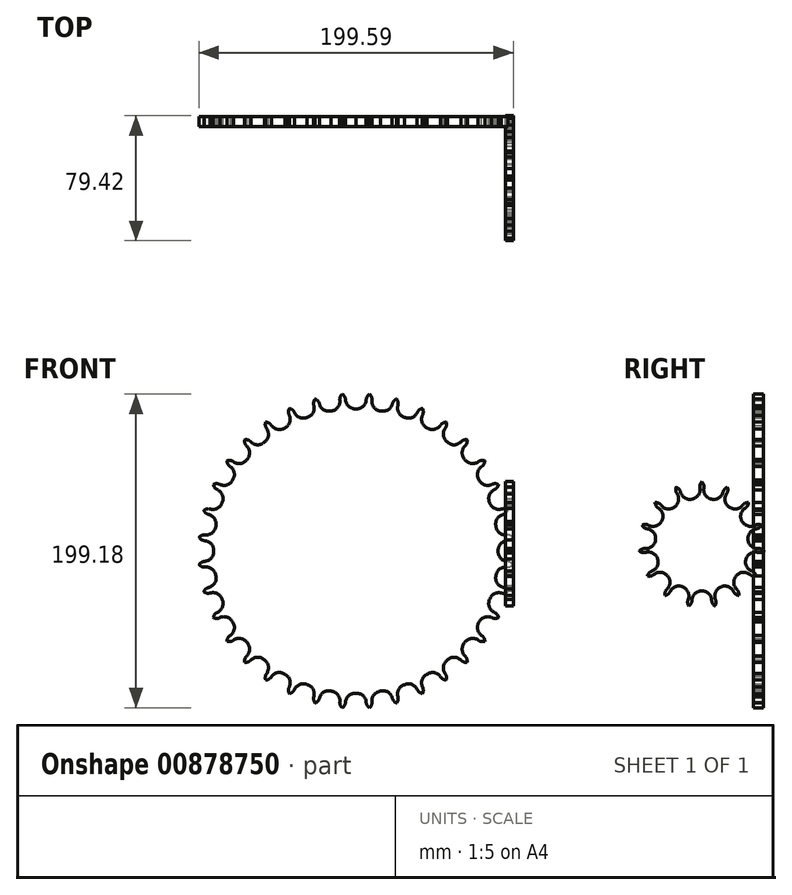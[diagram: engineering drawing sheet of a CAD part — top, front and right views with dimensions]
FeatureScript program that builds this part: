
annotation { "Feature Type Name" : "Feature", "Feature Type Description" : "" }
export const myFeature = defineFeature(function(context is Context, id is Id, definition is map)
    precondition{}
    {
        {
            var Q0;
            Q0=qCreatedBy(makeId("Right.planeOp"),FACE);
            cPlane(context, id + "F0", {"entities" : qUnion([Q0]), "cplaneType" : CPlaneType.OFFSET, "offset" : 95 * mm, "width" : 150 * mm, "height" : 150 * mm});
        }
        {
            var Q0;
            Q0=qCreatedBy(makeId("Front.planeOp"),FACE);
            var sketch = newSketch(context, id + "F1", { "sketchPlane" : qUnion([Q0])});
            skArc(sketch, "E0", {"start": v(-5.07, 74.25) * mm, "mid": v(-3.4, 71.1) * mm, "end": v(0, 70) * mm});
            skArc(sketch, "E1", {"start": v(-5.07, 74.25) * mm, "mid": v(-5.54, 75.94) * mm, "end": v(-6.79, 77.2) * mm});
            skSolve(sketch);
        }
        {
            var Q0;
            Q0=qCreatedBy(makeId("Front.planeOp"),FACE);
            var sketch = newSketch(context, id + "F2", { "sketchPlane" : qUnion([Q0])});
            skArc(sketch, "E2.0", {"start": v(20.63, -71.5) * mm, "mid": v(21.13, -67.97) * mm, "end": v(23.94, -65.78) * mm});
            skArc(sketch, "E2.1", {"start": v(7.9, -74) * mm, "mid": v(9, -70.6) * mm, "end": v(12.16, -68.94) * mm});
            skArc(sketch, "E2.2", {"start": v(51.6, -53.62) * mm, "mid": v(48.3, -52.28) * mm, "end": v(45, -53.62) * mm});
            skArc(sketch, "E2.3", {"start": v(68.04, 30.15) * mm, "mid": v(65.65, 27.5) * mm, "end": v(65.78, 23.94) * mm});
            skArc(sketch, "E2.4", {"start": v(-41.5, -61.77) * mm, "mid": v(-38.49, -59.87) * mm, "end": v(-35, -60.62) * mm});
            skArc(sketch, "E2.5", {"start": v(-17.88, -72.24) * mm, "mid": v(-15.69, -69.43) * mm, "end": v(-12.16, -68.94) * mm});
            skArc(sketch, "E2.6", {"start": v(-72.24, -17.88) * mm, "mid": v(-69.43, -15.69) * mm, "end": v(-68.94, -12.16) * mm});
            skArc(sketch, "E2.7", {"start": v(30.15, 68.04) * mm, "mid": v(27.5, 65.65) * mm, "end": v(23.94, 65.78) * mm});
            skArc(sketch, "E2.8", {"start": v(51.6, 53.62) * mm, "mid": v(48.3, 52.28) * mm, "end": v(45, 53.62) * mm});
            skArc(sketch, "E2.9", {"start": v(-74, 7.9) * mm, "mid": v(-70.6, 9) * mm, "end": v(-68.94, 12.16) * mm});
            skArc(sketch, "E2.10", {"start": v(43.84, -60.13) * mm, "mid": v(43.1, -56.64) * mm, "end": v(45, -53.62) * mm});
            skArc(sketch, "E2.11", {"start": v(32.74, 66.83) * mm, "mid": v(32.6, 63.27) * mm, "end": v(35, 60.62) * mm});
            skArc(sketch, "E2.12", {"start": v(-41.5, 61.77) * mm, "mid": v(-38.49, 59.87) * mm, "end": v(-35, 60.62) * mm});
            skArc(sketch, "E2.13", {"start": v(68.04, -30.15) * mm, "mid": v(65.65, -27.5) * mm, "end": v(65.78, -23.94) * mm});
            skArc(sketch, "E2.14", {"start": v(-61.77, -41.5) * mm, "mid": v(-59.87, -38.49) * mm, "end": v(-60.62, -35) * mm});
            skArc(sketch, "E2.15", {"start": v(-53.62, -51.6) * mm, "mid": v(-52.28, -48.3) * mm, "end": v(-53.62, -45) * mm});
            skArc(sketch, "E2.16", {"start": v(61.77, -41.5) * mm, "mid": v(59.87, -38.49) * mm, "end": v(60.62, -35) * mm});
            skArc(sketch, "E2.17", {"start": v(-43.84, -60.13) * mm, "mid": v(-43.1, -56.64) * mm, "end": v(-45, -53.62) * mm});
            skArc(sketch, "E2.18", {"start": v(-5.07, -74.25) * mm, "mid": v(-3.4, -71.1) * mm, "end": v(0, -70) * mm});
            skArc(sketch, "E2.19", {"start": v(53.62, -51.6) * mm, "mid": v(52.28, -48.3) * mm, "end": v(53.62, -45) * mm});
            skArc(sketch, "E2.20", {"start": v(41.5, 61.77) * mm, "mid": v(38.49, 59.87) * mm, "end": v(35, 60.62) * mm});
            skArc(sketch, "E2.21", {"start": v(53.62, 51.6) * mm, "mid": v(52.28, 48.3) * mm, "end": v(53.62, 45) * mm});
            skArc(sketch, "E2.22", {"start": v(-32.74, 66.83) * mm, "mid": v(-32.6, 63.27) * mm, "end": v(-35, 60.62) * mm});
            skArc(sketch, "E2.23", {"start": v(-60.13, 43.84) * mm, "mid": v(-56.64, 43.1) * mm, "end": v(-53.62, 45) * mm});
            skArc(sketch, "E2.24", {"start": v(17.88, -72.24) * mm, "mid": v(15.69, -69.43) * mm, "end": v(12.16, -68.94) * mm});
            skArc(sketch, "E2.25", {"start": v(60.13, 43.84) * mm, "mid": v(56.64, 43.1) * mm, "end": v(53.62, 45) * mm});
            skArc(sketch, "E2.26", {"start": v(72.24, -17.88) * mm, "mid": v(69.43, -15.69) * mm, "end": v(68.94, -12.16) * mm});
            skArc(sketch, "E2.27", {"start": v(-7.9, -74) * mm, "mid": v(-9, -70.6) * mm, "end": v(-12.16, -68.94) * mm});
            skArc(sketch, "E2.28", {"start": v(-66.83, 32.74) * mm, "mid": v(-63.27, 32.6) * mm, "end": v(-60.62, 35) * mm});
            skArc(sketch, "E2.29", {"start": v(-20.63, -71.5) * mm, "mid": v(-21.13, -67.97) * mm, "end": v(-23.94, -65.78) * mm});
            skArc(sketch, "E2.30", {"start": v(61.77, 41.5) * mm, "mid": v(59.87, 38.49) * mm, "end": v(60.62, 35) * mm});
            skArc(sketch, "E2.31", {"start": v(74.25, -5.07) * mm, "mid": v(71.1, -3.4) * mm, "end": v(70, 0) * mm});
            skArc(sketch, "E2.32", {"start": v(-72.24, 17.88) * mm, "mid": v(-69.43, 15.69) * mm, "end": v(-68.94, 12.16) * mm});
            skArc(sketch, "E2.33", {"start": v(-32.74, -66.83) * mm, "mid": v(-32.6, -63.27) * mm, "end": v(-35, -60.62) * mm});
            skArc(sketch, "E2.34", {"start": v(-74, -7.9) * mm, "mid": v(-70.6, -9) * mm, "end": v(-68.94, -12.16) * mm});
            skArc(sketch, "E2.35", {"start": v(-68.04, 30.15) * mm, "mid": v(-65.65, 27.5) * mm, "end": v(-65.78, 23.94) * mm});
            skArc(sketch, "E2.36", {"start": v(71.5, 20.63) * mm, "mid": v(67.97, 21.13) * mm, "end": v(65.78, 23.94) * mm});
            skArc(sketch, "E2.37", {"start": v(-71.5, -20.63) * mm, "mid": v(-67.97, -21.13) * mm, "end": v(-65.78, -23.94) * mm});
            skArc(sketch, "E2.38", {"start": v(60.13, -43.84) * mm, "mid": v(56.64, -43.1) * mm, "end": v(53.62, -45) * mm});
            skArc(sketch, "E2.39", {"start": v(41.5, -61.77) * mm, "mid": v(38.49, -59.87) * mm, "end": v(35, -60.62) * mm});
            skArc(sketch, "E2.40", {"start": v(-61.77, 41.5) * mm, "mid": v(-59.87, 38.49) * mm, "end": v(-60.62, 35) * mm});
            skArc(sketch, "E2.41", {"start": v(43.84, 60.13) * mm, "mid": v(43.1, 56.64) * mm, "end": v(45, 53.62) * mm});
            skArc(sketch, "E2.42", {"start": v(-66.83, -32.74) * mm, "mid": v(-63.27, -32.6) * mm, "end": v(-60.62, -35) * mm});
            skArc(sketch, "E2.43", {"start": v(71.5, -20.63) * mm, "mid": v(67.97, -21.13) * mm, "end": v(65.78, -23.94) * mm});
            skArc(sketch, "E2.44", {"start": v(-51.6, 53.62) * mm, "mid": v(-48.3, 52.28) * mm, "end": v(-45, 53.62) * mm});
            skArc(sketch, "E2.45", {"start": v(-17.88, 72.24) * mm, "mid": v(-15.69, 69.43) * mm, "end": v(-12.16, 68.94) * mm});
            skArc(sketch, "E2.46", {"start": v(72.24, 17.88) * mm, "mid": v(69.43, 15.69) * mm, "end": v(68.94, 12.16) * mm});
            skArc(sketch, "E2.47", {"start": v(66.83, 32.74) * mm, "mid": v(63.27, 32.6) * mm, "end": v(60.62, 35) * mm});
            skArc(sketch, "E2.48", {"start": v(-74.25, -5.07) * mm, "mid": v(-71.1, -3.4) * mm, "end": v(-70, 0) * mm});
            skArc(sketch, "E2.49", {"start": v(5.07, -74.25) * mm, "mid": v(3.4, -71.1) * mm, "end": v(0, -70) * mm});
            skArc(sketch, "E2.50", {"start": v(-30.15, -68.04) * mm, "mid": v(-27.5, -65.65) * mm, "end": v(-23.94, -65.78) * mm});
            skArc(sketch, "E2.51", {"start": v(30.15, -68.04) * mm, "mid": v(27.5, -65.65) * mm, "end": v(23.94, -65.78) * mm});
            skArc(sketch, "E2.52", {"start": v(-20.63, 71.5) * mm, "mid": v(-21.13, 67.97) * mm, "end": v(-23.94, 65.78) * mm});
            skArc(sketch, "E2.53", {"start": v(-53.62, 51.6) * mm, "mid": v(-52.28, 48.3) * mm, "end": v(-53.62, 45) * mm});
            skArc(sketch, "E2.54", {"start": v(-51.6, -53.62) * mm, "mid": v(-48.3, -52.28) * mm, "end": v(-45, -53.62) * mm});
            skArc(sketch, "E2.55", {"start": v(-60.13, -43.84) * mm, "mid": v(-56.64, -43.1) * mm, "end": v(-53.62, -45) * mm});
            skArc(sketch, "E2.56", {"start": v(74, 7.9) * mm, "mid": v(70.6, 9) * mm, "end": v(68.94, 12.16) * mm});
            skArc(sketch, "E2.57", {"start": v(-74.25, 5.07) * mm, "mid": v(-71.1, 3.4) * mm, "end": v(-70, 0) * mm});
            skArc(sketch, "E2.58", {"start": v(74, -7.9) * mm, "mid": v(70.6, -9) * mm, "end": v(68.94, -12.16) * mm});
            skArc(sketch, "E2.59", {"start": v(-43.84, 60.13) * mm, "mid": v(-43.1, 56.64) * mm, "end": v(-45, 53.62) * mm});
            skArc(sketch, "E2.60", {"start": v(-30.15, 68.04) * mm, "mid": v(-27.5, 65.65) * mm, "end": v(-23.94, 65.78) * mm});
            skArc(sketch, "E2.61", {"start": v(-71.5, 20.63) * mm, "mid": v(-67.97, 21.13) * mm, "end": v(-65.78, 23.94) * mm});
            skArc(sketch, "E2.62", {"start": v(32.74, -66.83) * mm, "mid": v(32.6, -63.27) * mm, "end": v(35, -60.62) * mm});
            skArc(sketch, "E2.63", {"start": v(-68.04, -30.15) * mm, "mid": v(-65.65, -27.5) * mm, "end": v(-65.78, -23.94) * mm});
            skArc(sketch, "E2.64", {"start": v(74.25, 5.07) * mm, "mid": v(71.1, 3.4) * mm, "end": v(70, 0) * mm});
            skArc(sketch, "E2.65", {"start": v(66.83, -32.74) * mm, "mid": v(63.27, -32.6) * mm, "end": v(60.62, -35) * mm});
            skArc(sketch, "E3.0", {"start": v(17.88, 72.24) * mm, "mid": v(15.69, 69.43) * mm, "end": v(12.16, 68.94) * mm});
            skArc(sketch, "E3.1", {"start": v(5.07, 74.25) * mm, "mid": v(3.4, 71.1) * mm, "end": v(0, 70) * mm});
            skArc(sketch, "E3.2", {"start": v(-7.9, 74) * mm, "mid": v(-9, 70.6) * mm, "end": v(-12.16, 68.94) * mm});
            skArc(sketch, "E3.3", {"start": v(-5.07, 74.25) * mm, "mid": v(-3.4, 71.1) * mm, "end": v(0, 70) * mm});
            skArc(sketch, "E3.4", {"start": v(7.9, 74) * mm, "mid": v(9, 70.6) * mm, "end": v(12.16, 68.94) * mm});
            skArc(sketch, "E3.6", {"start": v(20.63, 71.5) * mm, "mid": v(21.13, 67.97) * mm, "end": v(23.94, 65.78) * mm});
            skArc(sketch, "E4.0", {"start": v(20.63, 71.5) * mm, "mid": v(20.76, 73.26) * mm, "end": v(20.02, 74.86) * mm});
            skArc(sketch, "E5.0", {"start": v(17.88, 72.24) * mm, "mid": v(18.65, 73.83) * mm, "end": v(20.09, 74.84) * mm});
            skArc(sketch, "E6.0", {"start": v(7.9, 74) * mm, "mid": v(7.73, 75.75) * mm, "end": v(6.72, 77.2) * mm});
            skArc(sketch, "E7.0", {"start": v(5.07, 74.25) * mm, "mid": v(5.54, 75.94) * mm, "end": v(6.79, 77.2) * mm});
            skPoint(sketch, "E8.0", {"position": v(0, 0) * mm});
            skArc(sketch, "E9.0", {"start": v(-5.07, 74.25) * mm, "mid": v(-5.54, 75.94) * mm, "end": v(-6.79, 77.2) * mm});
            skArc(sketch, "E10.0", {"start": v(-7.9, 74) * mm, "mid": v(-7.73, 75.75) * mm, "end": v(-6.72, 77.2) * mm});
            skArc(sketch, "E11.0", {"start": v(-17.88, 72.24) * mm, "mid": v(-18.65, 73.83) * mm, "end": v(-20.09, 74.84) * mm});
            skArc(sketch, "E12.0", {"start": v(-20.63, 71.5) * mm, "mid": v(-20.76, 73.26) * mm, "end": v(-20.02, 74.86) * mm});
            skPoint(sketch, "E13.0", {"position": v(-31.19, 69.46) * mm});
            skArc(sketch, "E14.0", {"start": v(-30.15, 68.04) * mm, "mid": v(-31.18, 69.47) * mm, "end": v(-32.78, 70.21) * mm});
            skArc(sketch, "E15.0", {"start": v(-32.74, 66.83) * mm, "mid": v(-33.17, 68.54) * mm, "end": v(-32.72, 70.24) * mm});
            skArc(sketch, "E16.0", {"start": v(-41.5, 61.77) * mm, "mid": v(-42.77, 63) * mm, "end": v(-44.47, 63.45) * mm});
            skArc(sketch, "E17.0", {"start": v(-43.84, 60.13) * mm, "mid": v(-44.57, 61.74) * mm, "end": v(-44.42, 63.5) * mm});
            skArc(sketch, "E18.0", {"start": v(30.15, 68.04) * mm, "mid": v(31.18, 69.47) * mm, "end": v(32.78, 70.21) * mm});
            skArc(sketch, "E19.0", {"start": v(32.74, 66.83) * mm, "mid": v(33.17, 68.54) * mm, "end": v(32.72, 70.24) * mm});
            skArc(sketch, "E20.0", {"start": v(41.5, 61.77) * mm, "mid": v(42.77, 63) * mm, "end": v(44.47, 63.45) * mm});
            skArc(sketch, "E21.0", {"start": v(43.84, 60.13) * mm, "mid": v(44.57, 61.74) * mm, "end": v(44.42, 63.5) * mm});
            skArc(sketch, "E22.2", {"start": v(-60.13, 43.84) * mm, "mid": v(-61.74, 44.57) * mm, "end": v(-63.5, 44.42) * mm});
            skArc(sketch, "E23.0", {"start": v(-53.62, 51.6) * mm, "mid": v(-54.61, 53.06) * mm, "end": v(-54.77, 54.82) * mm});
            skArc(sketch, "E24.0", {"start": v(-51.6, 53.62) * mm, "mid": v(-53.06, 54.61) * mm, "end": v(-54.82, 54.77) * mm});
            skArc(sketch, "E25.0", {"start": v(-61.77, 41.5) * mm, "mid": v(-63, 42.77) * mm, "end": v(-63.45, 44.47) * mm});
            skArc(sketch, "E25.1", {"start": v(-66.83, 32.74) * mm, "mid": v(-68.54, 33.17) * mm, "end": v(-70.24, 32.72) * mm});
            skArc(sketch, "E25.2", {"start": v(-68.04, 30.15) * mm, "mid": v(-69.47, 31.18) * mm, "end": v(-70.21, 32.78) * mm});
            skArc(sketch, "E26.0", {"start": v(-72.24, -17.88) * mm, "mid": v(-73.83, -18.65) * mm, "end": v(-74.84, -20.09) * mm});
            skArc(sketch, "E26.1", {"start": v(-68.04, -30.15) * mm, "mid": v(-69.47, -31.18) * mm, "end": v(-70.21, -32.78) * mm});
            skArc(sketch, "E26.2", {"start": v(-71.5, -20.63) * mm, "mid": v(-73.26, -20.76) * mm, "end": v(-74.86, -20.02) * mm});
            skArc(sketch, "E26.3", {"start": v(-74, -7.9) * mm, "mid": v(-75.75, -7.73) * mm, "end": v(-77.2, -6.72) * mm});
            skArc(sketch, "E26.4", {"start": v(-71.5, 20.63) * mm, "mid": v(-73.26, 20.76) * mm, "end": v(-74.86, 20.02) * mm});
            skArc(sketch, "E26.5", {"start": v(-74, 7.9) * mm, "mid": v(-75.75, 7.73) * mm, "end": v(-77.2, 6.72) * mm});
            skArc(sketch, "E26.6", {"start": v(-72.24, 17.88) * mm, "mid": v(-73.83, 18.65) * mm, "end": v(-74.84, 20.09) * mm});
            skArc(sketch, "E26.7", {"start": v(-66.83, -32.74) * mm, "mid": v(-68.54, -33.17) * mm, "end": v(-70.24, -32.72) * mm});
            skArc(sketch, "E26.8", {"start": v(-74.25, -5.07) * mm, "mid": v(-75.94, -5.54) * mm, "end": v(-77.2, -6.79) * mm});
            skArc(sketch, "E26.9", {"start": v(-74.25, 5.07) * mm, "mid": v(-75.94, 5.54) * mm, "end": v(-77.2, 6.79) * mm});
            skArc(sketch, "E27.0", {"start": v(-43.84, -60.13) * mm, "mid": v(-44.57, -61.74) * mm, "end": v(-44.42, -63.5) * mm});
            skArc(sketch, "E27.1", {"start": v(30.15, -68.04) * mm, "mid": v(31.18, -69.47) * mm, "end": v(32.78, -70.21) * mm});
            skArc(sketch, "E27.2", {"start": v(5.07, -74.25) * mm, "mid": v(5.54, -75.94) * mm, "end": v(6.79, -77.2) * mm});
            skArc(sketch, "E27.3", {"start": v(41.5, -61.77) * mm, "mid": v(42.77, -63) * mm, "end": v(44.47, -63.45) * mm});
            skArc(sketch, "E27.4", {"start": v(43.84, -60.13) * mm, "mid": v(44.57, -61.74) * mm, "end": v(44.42, -63.5) * mm});
            skArc(sketch, "E27.5", {"start": v(-30.15, -68.04) * mm, "mid": v(-31.18, -69.47) * mm, "end": v(-32.78, -70.21) * mm});
            skArc(sketch, "E27.6", {"start": v(-61.77, -41.5) * mm, "mid": v(-63, -42.77) * mm, "end": v(-63.45, -44.47) * mm});
            skArc(sketch, "E27.7", {"start": v(20.63, -71.5) * mm, "mid": v(20.76, -73.26) * mm, "end": v(20.02, -74.86) * mm});
            skArc(sketch, "E27.8", {"start": v(-51.6, -53.62) * mm, "mid": v(-53.06, -54.61) * mm, "end": v(-54.82, -54.77) * mm});
            skArc(sketch, "E27.9", {"start": v(51.6, -53.62) * mm, "mid": v(53.06, -54.61) * mm, "end": v(54.82, -54.77) * mm});
            skArc(sketch, "E27.10", {"start": v(-41.5, -61.77) * mm, "mid": v(-42.77, -63) * mm, "end": v(-44.47, -63.45) * mm});
            skArc(sketch, "E27.11", {"start": v(7.9, -74) * mm, "mid": v(7.73, -75.75) * mm, "end": v(6.72, -77.2) * mm});
            skArc(sketch, "E27.12", {"start": v(53.62, -51.6) * mm, "mid": v(54.61, -53.06) * mm, "end": v(54.77, -54.82) * mm});
            skArc(sketch, "E27.13", {"start": v(17.88, -72.24) * mm, "mid": v(18.65, -73.83) * mm, "end": v(20.09, -74.84) * mm});
            skArc(sketch, "E27.14", {"start": v(-17.88, -72.24) * mm, "mid": v(-18.65, -73.83) * mm, "end": v(-20.09, -74.84) * mm});
            skArc(sketch, "E27.15", {"start": v(32.74, -66.83) * mm, "mid": v(33.17, -68.54) * mm, "end": v(32.72, -70.24) * mm});
            skArc(sketch, "E27.16", {"start": v(-7.9, -74) * mm, "mid": v(-7.73, -75.75) * mm, "end": v(-6.72, -77.2) * mm});
            skArc(sketch, "E27.17", {"start": v(61.77, -41.5) * mm, "mid": v(63, -42.77) * mm, "end": v(63.45, -44.47) * mm});
            skArc(sketch, "E27.18", {"start": v(60.13, -43.84) * mm, "mid": v(61.74, -44.57) * mm, "end": v(63.5, -44.42) * mm});
            skArc(sketch, "E27.19", {"start": v(-5.07, -74.25) * mm, "mid": v(-5.54, -75.94) * mm, "end": v(-6.79, -77.2) * mm});
            skArc(sketch, "E27.20", {"start": v(-32.74, -66.83) * mm, "mid": v(-33.17, -68.54) * mm, "end": v(-32.72, -70.24) * mm});
            skArc(sketch, "E27.21", {"start": v(-53.62, -51.6) * mm, "mid": v(-54.61, -53.06) * mm, "end": v(-54.77, -54.82) * mm});
            skArc(sketch, "E27.22", {"start": v(-60.13, -43.84) * mm, "mid": v(-61.74, -44.57) * mm, "end": v(-63.5, -44.42) * mm});
            skArc(sketch, "E27.23", {"start": v(-20.63, -71.5) * mm, "mid": v(-20.76, -73.26) * mm, "end": v(-20.02, -74.86) * mm});
            skArc(sketch, "E28.0", {"start": v(74, -7.9) * mm, "mid": v(75.75, -7.73) * mm, "end": v(77.2, -6.72) * mm});
            skArc(sketch, "E28.1", {"start": v(68.04, -30.15) * mm, "mid": v(69.47, -31.18) * mm, "end": v(70.21, -32.78) * mm});
            skArc(sketch, "E28.2", {"start": v(66.83, 32.74) * mm, "mid": v(68.54, 33.17) * mm, "end": v(70.24, 32.72) * mm});
            skArc(sketch, "E28.3", {"start": v(72.24, -17.88) * mm, "mid": v(73.83, -18.65) * mm, "end": v(74.84, -20.09) * mm});
            skArc(sketch, "E28.4", {"start": v(74, 7.9) * mm, "mid": v(75.75, 7.73) * mm, "end": v(77.2, 6.72) * mm});
            skArc(sketch, "E28.5", {"start": v(71.5, 20.63) * mm, "mid": v(73.26, 20.76) * mm, "end": v(74.86, 20.02) * mm});
            skArc(sketch, "E28.6", {"start": v(71.5, -20.63) * mm, "mid": v(73.26, -20.76) * mm, "end": v(74.86, -20.02) * mm});
            skArc(sketch, "E28.7", {"start": v(74.25, -5.07) * mm, "mid": v(75.94, -5.54) * mm, "end": v(77.2, -6.79) * mm});
            skArc(sketch, "E28.8", {"start": v(66.83, -32.74) * mm, "mid": v(68.54, -33.17) * mm, "end": v(70.24, -32.72) * mm});
            skArc(sketch, "E28.9", {"start": v(74.25, 5.07) * mm, "mid": v(75.94, 5.54) * mm, "end": v(77.2, 6.79) * mm});
            skArc(sketch, "E28.10", {"start": v(68.04, 30.15) * mm, "mid": v(69.47, 31.18) * mm, "end": v(70.21, 32.78) * mm});
            skArc(sketch, "E28.11", {"start": v(72.24, 17.88) * mm, "mid": v(73.83, 18.65) * mm, "end": v(74.84, 20.09) * mm});
            skArc(sketch, "E29.0", {"start": v(51.6, 53.62) * mm, "mid": v(53.06, 54.61) * mm, "end": v(54.82, 54.77) * mm});
            skArc(sketch, "E29.1", {"start": v(53.62, 51.6) * mm, "mid": v(54.61, 53.06) * mm, "end": v(54.77, 54.82) * mm});
            skArc(sketch, "E29.2", {"start": v(78.58, 56.75) * mm, "mid": v(80.19, 57.47) * mm, "end": v(81.94, 57.32) * mm});
            skArc(sketch, "E29.3", {"start": v(61.77, 41.5) * mm, "mid": v(63, 42.77) * mm, "end": v(63.45, 44.47) * mm});
            skArc(sketch, "E29.12", {"start": v(60.13, 43.84) * mm, "mid": v(61.74, 44.57) * mm, "end": v(63.5, 44.42) * mm});
            skSolve(sketch);
        }
        {
            var Q0;
            {var subQ51=sQuery(id+"F2.wireOp",EDGE,"E2.14");Q0=makeQuery(id+"F2.imprint","IMPRINT",FACE,{"disambiguationData":[TD([[makeQuery(id+"F2.imprint","IMPRINT",EDGE,{"derivedFrom":subQ51}),-1.0]])]});}
            extrude(context, id + "F3", {"entities" : qUnion([Q0]), "depth" : 5 * mm, "offsetDistance" : 25 * mm});
        }
        {
            var Q0;
            {var subQ51=sQuery(id+"F2.wireOp",EDGE,"E2.14");Q0=makeQuery(id+"F2.imprint","IMPRINT",FACE,{"disambiguationData":[TD([[makeQuery(id+"F2.imprint","IMPRINT",EDGE,{"derivedFrom":subQ51}),-1.0]])]});}
            extrude(context, id + "F4", {"entities" : qUnion([Q0]), "operationType" : NewBodyOperationType.ADD, "depth" : 3.87 * mm, "offsetDistance" : 25 * mm});
        }
        {
            var Q0;
            Q0=makeQuery(id+"F3.opExtrude","SWEPT_BODY",BODY,{"disambiguationData":[OSD([sQuery(id+"F2.wireOp",EDGE,"E2.14"),sQuery(id+"F2.wireOp",EDGE,"E2.16"),sQuery(id+"F2.wireOp",EDGE,"E2.42"),sQuery(id+"F2.wireOp",EDGE,"E2.60"),sQuery(id+"F2.wireOp",EDGE,"E2.63"),sQuery(id+"F2.wireOp",EDGE,"E3.0"),sQuery(id+"F2.wireOp",EDGE,"E3.1"),sQuery(id+"F2.wireOp",EDGE,"E3.2"),sQuery(id+"F2.wireOp",EDGE,"E3.3"),sQuery(id+"F2.wireOp",EDGE,"E3.4"),sQuery(id+"F2.wireOp",EDGE,"E3.6"),sQuery(id+"F2.wireOp",EDGE,"E2.7"),sQuery(id+"F2.wireOp",EDGE,"E2.12"),sQuery(id+"F2.wireOp",EDGE,"E2.20"),sQuery(id+"F2.wireOp",EDGE,"E2.22"),sQuery(id+"F2.wireOp",EDGE,"E2.25"),sQuery(id+"F2.wireOp",EDGE,"E2.26"),sQuery(id+"F2.wireOp",EDGE,"E2.32"),sQuery(id+"F2.wireOp",EDGE,"E2.35"),sQuery(id+"F2.wireOp",EDGE,"E2.41"),sQuery(id+"F2.wireOp",EDGE,"E2.44"),sQuery(id+"F2.wireOp",EDGE,"E2.45"),sQuery(id+"F2.wireOp",EDGE,"E2.48"),sQuery(id+"F2.wireOp",EDGE,"E2.52"),sQuery(id+"F2.wireOp",EDGE,"E2.59"),sQuery(id+"F2.wireOp",EDGE,"E2.64"),sQuery(id+"F2.wireOp",EDGE,"E4.0"),sQuery(id+"F2.wireOp",EDGE,"E5.0"),sQuery(id+"F2.wireOp",EDGE,"E6.0"),sQuery(id+"F2.wireOp",EDGE,"E7.0"),sQuery(id+"F2.wireOp",EDGE,"E9.0"),sQuery(id+"F2.wireOp",EDGE,"E10.0"),sQuery(id+"F2.wireOp",EDGE,"E11.0"),sQuery(id+"F2.wireOp",EDGE,"E12.0"),sQuery(id+"F2.wireOp",EDGE,"E14.0"),sQuery(id+"F2.wireOp",EDGE,"E15.0"),sQuery(id+"F2.wireOp",EDGE,"E16.0"),sQuery(id+"F2.wireOp",EDGE,"E17.0"),sQuery(id+"F2.wireOp",EDGE,"E18.0"),sQuery(id+"F2.wireOp",EDGE,"E19.0"),sQuery(id+"F2.wireOp",EDGE,"E2.23"),sQuery(id+"F2.wireOp",EDGE,"E2.53"),sQuery(id+"F2.wireOp",EDGE,"E24.0"),sQuery(id+"F2.wireOp",EDGE,"E23.0"),sQuery(id+"F2.wireOp",EDGE,"E25.0"),sQuery(id+"F2.wireOp",EDGE,"E25.1"),sQuery(id+"F2.wireOp",EDGE,"E25.2"),sQuery(id+"F2.wireOp",EDGE,"E2.28"),sQuery(id+"F2.wireOp",EDGE,"E2.40"),sQuery(id+"F2.wireOp",EDGE,"E22.2"),sQuery(id+"F2.wireOp",EDGE,"E26.0"),sQuery(id+"F2.wireOp",EDGE,"E26.1"),sQuery(id+"F2.wireOp",EDGE,"E26.2"),sQuery(id+"F2.wireOp",EDGE,"E26.3"),sQuery(id+"F2.wireOp",EDGE,"E26.4"),sQuery(id+"F2.wireOp",EDGE,"E26.5"),sQuery(id+"F2.wireOp",EDGE,"E26.6"),sQuery(id+"F2.wireOp",EDGE,"E26.7"),sQuery(id+"F2.wireOp",EDGE,"E26.8"),sQuery(id+"F2.wireOp",EDGE,"E26.9"),sQuery(id+"F2.wireOp",EDGE,"E2.6"),sQuery(id+"F2.wireOp",EDGE,"E2.9"),sQuery(id+"F2.wireOp",EDGE,"E2.34"),sQuery(id+"F2.wireOp",EDGE,"E2.37"),sQuery(id+"F2.wireOp",EDGE,"E2.57"),sQuery(id+"F2.wireOp",EDGE,"E2.61"),sQuery(id+"F2.wireOp",EDGE,"E27.0"),sQuery(id+"F2.wireOp",EDGE,"E27.1"),sQuery(id+"F2.wireOp",EDGE,"E27.2"),sQuery(id+"F2.wireOp",EDGE,"E27.3"),sQuery(id+"F2.wireOp",EDGE,"E27.4"),sQuery(id+"F2.wireOp",EDGE,"E27.5"),sQuery(id+"F2.wireOp",EDGE,"E27.6"),sQuery(id+"F2.wireOp",EDGE,"E27.7"),sQuery(id+"F2.wireOp",EDGE,"E27.8"),sQuery(id+"F2.wireOp",EDGE,"E27.9"),sQuery(id+"F2.wireOp",EDGE,"E27.10"),sQuery(id+"F2.wireOp",EDGE,"E27.11"),sQuery(id+"F2.wireOp",EDGE,"E27.12"),sQuery(id+"F2.wireOp",EDGE,"E27.13"),sQuery(id+"F2.wireOp",EDGE,"E27.14"),sQuery(id+"F2.wireOp",EDGE,"E27.15"),sQuery(id+"F2.wireOp",EDGE,"E27.16"),sQuery(id+"F2.wireOp",EDGE,"E27.17"),sQuery(id+"F2.wireOp",EDGE,"E27.18"),sQuery(id+"F2.wireOp",EDGE,"E27.19"),sQuery(id+"F2.wireOp",EDGE,"E27.20"),sQuery(id+"F2.wireOp",EDGE,"E27.21"),sQuery(id+"F2.wireOp",EDGE,"E27.22"),sQuery(id+"F2.wireOp",EDGE,"E27.23"),sQuery(id+"F2.wireOp",EDGE,"E2.0"),sQuery(id+"F2.wireOp",EDGE,"E2.1"),sQuery(id+"F2.wireOp",EDGE,"E2.2"),sQuery(id+"F2.wireOp",EDGE,"E2.4"),sQuery(id+"F2.wireOp",EDGE,"E2.5"),sQuery(id+"F2.wireOp",EDGE,"E2.10"),sQuery(id+"F2.wireOp",EDGE,"E2.15"),sQuery(id+"F2.wireOp",EDGE,"E2.17"),sQuery(id+"F2.wireOp",EDGE,"E2.18"),sQuery(id+"F2.wireOp",EDGE,"E2.19"),sQuery(id+"F2.wireOp",EDGE,"E2.24"),sQuery(id+"F2.wireOp",EDGE,"E2.27"),sQuery(id+"F2.wireOp",EDGE,"E2.29"),sQuery(id+"F2.wireOp",EDGE,"E2.33"),sQuery(id+"F2.wireOp",EDGE,"E2.38"),sQuery(id+"F2.wireOp",EDGE,"E2.39"),sQuery(id+"F2.wireOp",EDGE,"E2.49"),sQuery(id+"F2.wireOp",EDGE,"E2.50"),sQuery(id+"F2.wireOp",EDGE,"E2.51"),sQuery(id+"F2.wireOp",EDGE,"E2.54"),sQuery(id+"F2.wireOp",EDGE,"E2.55"),sQuery(id+"F2.wireOp",EDGE,"E2.62"),sQuery(id+"F2.wireOp",EDGE,"E28.0"),sQuery(id+"F2.wireOp",EDGE,"E28.1"),sQuery(id+"F2.wireOp",EDGE,"E28.3"),sQuery(id+"F2.wireOp",EDGE,"E28.4"),sQuery(id+"F2.wireOp",EDGE,"E28.5"),sQuery(id+"F2.wireOp",EDGE,"E28.6"),sQuery(id+"F2.wireOp",EDGE,"E28.7"),sQuery(id+"F2.wireOp",EDGE,"E28.8"),sQuery(id+"F2.wireOp",EDGE,"E28.9"),sQuery(id+"F2.wireOp",EDGE,"E28.11"),sQuery(id+"F2.wireOp",EDGE,"E2.3"),sQuery(id+"F2.wireOp",EDGE,"E2.13"),sQuery(id+"F2.wireOp",EDGE,"E2.31"),sQuery(id+"F2.wireOp",EDGE,"E2.36"),sQuery(id+"F2.wireOp",EDGE,"E2.43"),sQuery(id+"F2.wireOp",EDGE,"E2.46"),sQuery(id+"F2.wireOp",EDGE,"E2.56"),sQuery(id+"F2.wireOp",EDGE,"E2.58"),sQuery(id+"F2.wireOp",EDGE,"E2.65"),sQuery(id+"F2.wireOp",EDGE,"E29.0"),sQuery(id+"F2.wireOp",EDGE,"E29.1"),sQuery(id+"F2.wireOp",EDGE,"E29.3"),sQuery(id+"F2.wireOp",EDGE,"E2.8"),sQuery(id+"F2.wireOp",EDGE,"E2.11"),sQuery(id+"F2.wireOp",EDGE,"E2.21"),sQuery(id+"F2.wireOp",EDGE,"E28.2"),sQuery(id+"F2.wireOp",EDGE,"E21.0"),sQuery(id+"F2.wireOp",EDGE,"E2.30"),sQuery(id+"F2.wireOp",EDGE,"E20.0"),sQuery(id+"F2.wireOp",EDGE,"E28.10"),sQuery(id+"F2.wireOp",EDGE,"E29.12"),sQuery(id+"F2.wireOp",EDGE,"E2.47")])]});
            var Q1;
            Q1=sQuery(id+"F2.wireOp",VERTEX,"E8.0");
            transform(context, id + "F5", {"entities" : qUnion([Q0]), "transformType" : TransformType.SCALE_UNIFORMLY, "scale" : 1.3, "scalePoint" : qUnion([Q1]), "makeCopy" : false});
        }
        {
            var Q0;
            Q0=qCreatedBy(makeId("Right.planeOp"),FACE);
            var sketch = newSketch(context, id + "F6", { "sketchPlane" : qUnion([Q0])});
            skArc(sketch, "E30", {"start": v(0, 36.48) * mm, "mid": v(1.7, 37.15) * mm, "end": v(2.82, 38.58) * mm});
            skArc(sketch, "E31", {"start": v(4.2, 39.72) * mm, "mid": v(3.26, 39.45) * mm, "end": v(2.82, 38.58) * mm});
            skSolve(sketch);
        }
        {
            var Q0;
            Q0=qCreatedBy(makeId("Front.planeOp"),FACE);
            var sketch = newSketch(context, id + "F7", { "sketchPlane" : qUnion([Q0])});
            skLineSegment(sketch, "E32", {"start": v(46.12, 0) * mm, "end": v(-35.6, 0) * mm});
            skSolve(sketch);
        }
        {
            var Q0;
            {var subQ0=sQuery(id+"FuSN5E2cZiAuNOm_3.wireOp",EDGE,"ce970788-27e3-47bc-be1a-0d92f62c386a.16");var subQ1=makeQuery(id+"FuSN5E2cZiAuNOm_3.imprint","INTERSECT",VERTEX,{"derivedFrom":[sQuery(id+"FuSN5E2cZiAuNOm_3.wireOp",EDGE,"57e1b842-f4a4-4b15-bf3c-e8c0f55d15c8.111"),subQ0]});Q0=makeQuery(id+"FuSN5E2cZiAuNOm_3.imprint","IMPRINT",FACE,{"disambiguationData":[TD([[makeQuery(id+"FuSN5E2cZiAuNOm_3.imprint","IMPRINT",EDGE,{"disambiguationData":[TD([[subQ1,-1.0]])],"derivedFrom":subQ0}),1.0]])]});}
            var sketch = newSketch(context, id + "F8", { "sketchPlane" : qUnion([Q0])});
            skArc(sketch, "E33.0", {"start": v(21.98, -28.21) * mm, "mid": v(20.25, -23.99) * mm, "end": v(21.93, -19.74) * mm});
            skArc(sketch, "E34.0", {"start": v(21.98, -28.21) * mm, "mid": v(23.25, -30.07) * mm, "end": v(23.47, -32.3) * mm});
            skPoint(sketch, "E35.0", {"position": v(29.43, -27) * mm});
            skPoint(sketch, "E36.0", {"position": v(29.92, -26.44) * mm});
            skLineSegment(sketch, "E37", {"start": v(29.43, -27) * mm, "end": v(29.92, -26.44) * mm});
            skLineSegment(sketch, "E38", {"start": v(29.67, -26.72) * mm, "end": v(0, 0) * mm});
            skPoint(sketch, "E39.0", {"position": v(23.77, -32.09) * mm});
            skLineSegment(sketch, "E40", {"start": v(23.17, -32.52) * mm, "end": v(23.77, -32.09) * mm});
            skLineSegment(sketch, "E41", {"start": v(23.47, -32.3) * mm, "end": v(23.98, -33) * mm});
            skArc(sketch, "E42.MirrorCS", {"start": v(30.36, -18.91) * mm, "mid": v(25.97, -17.63) * mm, "end": v(21.93, -19.74) * mm});
            skArc(sketch, "E43.MirrorCS", {"start": v(30.36, -18.91) * mm, "mid": v(32.33, -19.98) * mm, "end": v(34.58, -19.96) * mm});
            skSolve(sketch);
        }
        {
            var Q0;
            Q0=qCreatedBy(id+"F0.planeOp",FACE);
            var sketch = newSketch(context, id + "F9", { "sketchPlane" : qUnion([Q0])});
            skArc(sketch, "E44.0", {"start": v(-33.62, 12.19) * mm, "mid": v(-29.07, 11.85) * mm, "end": v(-25.55, 14.75) * mm});
            skArc(sketch, "E45.0", {"start": v(-27.37, 23.03) * mm, "mid": v(-24.8, 19.25) * mm, "end": v(-25.55, 14.75) * mm});
            skPoint(sketch, "E46.0", {"position": v(-28.99, 24.58) * mm});
            skArc(sketch, "E47.0", {"start": v(-27.37, 23.03) * mm, "mid": v(-29, 24.58) * mm, "end": v(-29.67, 26.72) * mm});
            skArc(sketch, "E48.0", {"start": v(-25.76, 24.8) * mm, "mid": v(-27.47, 26.27) * mm, "end": v(-29.67, 26.72) * mm});
            skArc(sketch, "E49.0", {"start": v(-25.76, 24.8) * mm, "mid": v(-21.74, 22.65) * mm, "end": v(-17.34, 23.87) * mm});
            skArc(sketch, "E50.0", {"start": v(-15.63, 32.17) * mm, "mid": v(-14.82, 27.68) * mm, "end": v(-17.34, 23.87) * mm});
            skArc(sketch, "E51.0", {"start": v(-15.63, 32.17) * mm, "mid": v(-16.5, 34.24) * mm, "end": v(-16.24, 36.48) * mm});
            skPoint(sketch, "E52.0", {"position": v(-14.42, 35.17) * mm});
            skArc(sketch, "E53.0", {"start": v(-13.44, 33.14) * mm, "mid": v(-10.65, 29.53) * mm, "end": v(-6.14, 28.86) * mm});
            skArc(sketch, "E54.0", {"start": v(-1.2, 35.74) * mm, "mid": v(-2.28, 31.31) * mm, "end": v(-6.14, 28.86) * mm});
            skArc(sketch, "E55.0", {"start": v(-1.2, 35.74) * mm, "mid": v(-1.14, 38) * mm, "end": v(0, 39.93) * mm});
            skPoint(sketch, "E56.0", {"position": v(1.13, 37.99) * mm});
            skArc(sketch, "E57.0", {"start": v(-13.44, 33.14) * mm, "mid": v(-14.41, 35.17) * mm, "end": v(-16.24, 36.48) * mm});
            skArc(sketch, "E58.0", {"start": v(1.2, 35.74) * mm, "mid": v(2.28, 31.31) * mm, "end": v(6.14, 28.86) * mm});
            skArc(sketch, "E59.0", {"start": v(1.2, 35.74) * mm, "mid": v(1.14, 38) * mm, "end": v(0, 39.93) * mm});
            skArc(sketch, "E60.0", {"start": v(13.44, 33.14) * mm, "mid": v(10.65, 29.53) * mm, "end": v(6.14, 28.86) * mm});
            skPoint(sketch, "E61.0", {"position": v(14.42, 35.17) * mm});
            skArc(sketch, "E62.0", {"start": v(13.44, 33.14) * mm, "mid": v(14.41, 35.17) * mm, "end": v(16.24, 36.48) * mm});
            skArc(sketch, "E63.0", {"start": v(15.63, 32.17) * mm, "mid": v(16.5, 34.24) * mm, "end": v(16.24, 36.48) * mm});
            skArc(sketch, "E64.0", {"start": v(15.63, 32.17) * mm, "mid": v(14.82, 27.68) * mm, "end": v(17.34, 23.87) * mm});
            skArc(sketch, "E65.0", {"start": v(25.76, 24.8) * mm, "mid": v(21.74, 22.65) * mm, "end": v(17.34, 23.87) * mm});
            skArc(sketch, "E66.0", {"start": v(27.37, 23.03) * mm, "mid": v(29, 24.58) * mm, "end": v(29.67, 26.72) * mm});
            skArc(sketch, "E67.0", {"start": v(27.37, 23.03) * mm, "mid": v(24.8, 19.25) * mm, "end": v(25.55, 14.75) * mm});
            skArc(sketch, "E68.0", {"start": v(33.62, 12.19) * mm, "mid": v(29.07, 11.85) * mm, "end": v(25.55, 14.75) * mm});
            skArc(sketch, "E69.0", {"start": v(25.76, 24.8) * mm, "mid": v(27.47, 26.27) * mm, "end": v(29.67, 26.72) * mm});
            skArc(sketch, "E70.0", {"start": v(33.62, 12.19) * mm, "mid": v(35.78, 12.82) * mm, "end": v(37.97, 12.34) * mm});
            skArc(sketch, "E71.0", {"start": v(34.36, 9.9) * mm, "mid": v(36.48, 10.66) * mm, "end": v(37.97, 12.34) * mm});
            skArc(sketch, "E72.0", {"start": v(34.36, 9.9) * mm, "mid": v(30.48, 7.5) * mm, "end": v(29.35, 3.08) * mm});
            skArc(sketch, "E73.0", {"start": v(-33.62, 12.19) * mm, "mid": v(-35.78, 12.82) * mm, "end": v(-37.97, 12.34) * mm});
            skArc(sketch, "E74.0", {"start": v(-34.36, 9.9) * mm, "mid": v(-36.48, 10.66) * mm, "end": v(-37.97, 12.34) * mm});
            skArc(sketch, "E75.0", {"start": v(-34.36, 9.9) * mm, "mid": v(-30.48, 7.5) * mm, "end": v(-29.35, 3.08) * mm});
            skArc(sketch, "E76.0", {"start": v(-35.67, -2.54) * mm, "mid": v(-31.38, -1) * mm, "end": v(-29.35, 3.08) * mm});
            skPoint(sketch, "E77.0", {"position": v(-37.9, -2.84) * mm});
            skArc(sketch, "E78.0", {"start": v(-35.67, -2.54) * mm, "mid": v(-37.9, -2.84) * mm, "end": v(-39.7, -4.17) * mm});
            skArc(sketch, "E79.0", {"start": v(-35.42, -4.93) * mm, "mid": v(-37.66, -5.1) * mm, "end": v(-39.7, -4.17) * mm});
            skArc(sketch, "E80.0", {"start": v(-35.42, -4.93) * mm, "mid": v(-30.9, -5.54) * mm, "end": v(-28.06, -9.12) * mm});
            skArc(sketch, "E81.0", {"start": v(-31.55, -16.83) * mm, "mid": v(-28.26, -13.68) * mm, "end": v(-28.06, -9.12) * mm});
            skArc(sketch, "E82.0", {"start": v(-31.55, -16.83) * mm, "mid": v(-33.47, -18.01) * mm, "end": v(-34.58, -19.96) * mm});
            skArc(sketch, "E83.0", {"start": v(-30.36, -18.91) * mm, "mid": v(-32.33, -19.98) * mm, "end": v(-34.58, -19.96) * mm});
            skArc(sketch, "E84.0", {"start": v(-30.36, -18.91) * mm, "mid": v(-25.97, -17.63) * mm, "end": v(-21.93, -19.74) * mm});
            skArc(sketch, "E85.0", {"start": v(-21.98, -28.21) * mm, "mid": v(-20.25, -23.99) * mm, "end": v(-21.93, -19.74) * mm});
            skPoint(sketch, "E86.0", {"position": v(-23.25, -30.07) * mm});
            skArc(sketch, "E87.0", {"start": v(-21.98, -28.21) * mm, "mid": v(-23.25, -30.07) * mm, "end": v(-23.47, -32.3) * mm});
            skPoint(sketch, "E88.0", {"position": v(-21.41, -31.4) * mm});
            skArc(sketch, "E89.0", {"start": v(-20.04, -29.62) * mm, "mid": v(-16.56, -26.67) * mm, "end": v(-12, -26.96) * mm});
            skArc(sketch, "E90.0", {"start": v(-20.04, -29.62) * mm, "mid": v(-21.4, -31.4) * mm, "end": v(-23.47, -32.3) * mm});
            skArc(sketch, "E91.0", {"start": v(-8.6, -34.71) * mm, "mid": v(-8.74, -30.15) * mm, "end": v(-12, -26.96) * mm});
            skArc(sketch, "E92.0", {"start": v(-8.6, -34.71) * mm, "mid": v(-9.01, -36.92) * mm, "end": v(-8.3, -39.06) * mm});
            skArc(sketch, "E93.0", {"start": v(-6.26, -35.21) * mm, "mid": v(-6.79, -37.4) * mm, "end": v(-8.3, -39.06) * mm});
            skArc(sketch, "E94.0", {"start": v(-6.26, -35.21) * mm, "mid": v(-4.28, -31.1) * mm, "end": v(0, -29.5) * mm});
            skArc(sketch, "E95.0", {"start": v(6.26, -35.21) * mm, "mid": v(4.28, -31.1) * mm, "end": v(0, -29.5) * mm});
            skArc(sketch, "E96.0", {"start": v(6.26, -35.21) * mm, "mid": v(6.79, -37.4) * mm, "end": v(8.3, -39.06) * mm});
            skArc(sketch, "E97.0", {"start": v(8.6, -34.71) * mm, "mid": v(9.01, -36.92) * mm, "end": v(8.3, -39.06) * mm});
            skArc(sketch, "E98.0", {"start": v(8.6, -34.71) * mm, "mid": v(8.74, -30.15) * mm, "end": v(12, -26.96) * mm});
            skArc(sketch, "E99.0", {"start": v(20.04, -29.62) * mm, "mid": v(16.56, -26.67) * mm, "end": v(12, -26.96) * mm});
            skArc(sketch, "E100.0", {"start": v(20.04, -29.62) * mm, "mid": v(21.4, -31.4) * mm, "end": v(23.47, -32.3) * mm});
            skArc(sketch, "E101.0", {"start": v(21.98, -28.21) * mm, "mid": v(23.25, -30.07) * mm, "end": v(23.47, -32.3) * mm});
            skArc(sketch, "E102.0", {"start": v(21.98, -28.21) * mm, "mid": v(20.25, -23.99) * mm, "end": v(21.93, -19.74) * mm});
            skArc(sketch, "E103.0", {"start": v(30.36, -18.91) * mm, "mid": v(25.97, -17.63) * mm, "end": v(21.93, -19.74) * mm});
            skArc(sketch, "E104.0", {"start": v(30.36, -18.91) * mm, "mid": v(32.33, -19.98) * mm, "end": v(34.58, -19.96) * mm});
            skArc(sketch, "E105.0", {"start": v(31.55, -16.83) * mm, "mid": v(33.47, -18.01) * mm, "end": v(34.58, -19.96) * mm});
            skArc(sketch, "E106.0", {"start": v(31.55, -16.83) * mm, "mid": v(28.26, -13.68) * mm, "end": v(28.06, -9.12) * mm});
            skArc(sketch, "E107.0", {"start": v(35.42, -4.93) * mm, "mid": v(30.9, -5.54) * mm, "end": v(28.06, -9.12) * mm});
            skPoint(sketch, "E108.0", {"position": v(37.66, -5.1) * mm});
            skArc(sketch, "E109.0", {"start": v(35.42, -4.93) * mm, "mid": v(37.66, -5.1) * mm, "end": v(39.7, -4.17) * mm});
            skArc(sketch, "E110.0", {"start": v(35.67, -2.54) * mm, "mid": v(37.9, -2.84) * mm, "end": v(39.7, -4.17) * mm});
            skArc(sketch, "E111.0", {"start": v(35.67, -2.54) * mm, "mid": v(31.38, -1) * mm, "end": v(29.35, 3.08) * mm});
            skSolve(sketch);
        }
        {
            var Q0;
            Q0 = qSketchRegion(id + "F9", true);
            extrude(context, id + "F10", {"entities" : qUnion([Q0]), "depth" : 5 * mm, "offsetDistance" : 25 * mm});
        }
        {
            var Q0;
            Q0=makeQuery(id+"F10.opExtrude","SWEPT_BODY",BODY,{"disambiguationData":[OSD([sQuery(id+"F9.wireOp",EDGE,"E44.0"),sQuery(id+"F9.wireOp",EDGE,"E45.0"),sQuery(id+"F9.wireOp",EDGE,"E47.0"),sQuery(id+"F9.wireOp",EDGE,"E48.0"),sQuery(id+"F9.wireOp",EDGE,"E49.0"),sQuery(id+"F9.wireOp",EDGE,"E50.0"),sQuery(id+"F9.wireOp",EDGE,"E51.0"),sQuery(id+"F9.wireOp",EDGE,"E53.0"),sQuery(id+"F9.wireOp",EDGE,"E54.0"),sQuery(id+"F9.wireOp",EDGE,"E55.0"),sQuery(id+"F9.wireOp",EDGE,"E57.0"),sQuery(id+"F9.wireOp",EDGE,"E58.0"),sQuery(id+"F9.wireOp",EDGE,"E59.0"),sQuery(id+"F9.wireOp",EDGE,"E60.0"),sQuery(id+"F9.wireOp",EDGE,"E62.0"),sQuery(id+"F9.wireOp",EDGE,"E63.0"),sQuery(id+"F9.wireOp",EDGE,"E64.0"),sQuery(id+"F9.wireOp",EDGE,"E65.0"),sQuery(id+"F9.wireOp",EDGE,"E66.0"),sQuery(id+"F9.wireOp",EDGE,"E67.0"),sQuery(id+"F9.wireOp",EDGE,"E68.0"),sQuery(id+"F9.wireOp",EDGE,"E69.0"),sQuery(id+"F9.wireOp",EDGE,"E70.0"),sQuery(id+"F9.wireOp",EDGE,"E71.0"),sQuery(id+"F9.wireOp",EDGE,"E72.0"),sQuery(id+"F9.wireOp",EDGE,"E73.0"),sQuery(id+"F9.wireOp",EDGE,"E74.0"),sQuery(id+"F9.wireOp",EDGE,"E75.0"),sQuery(id+"F9.wireOp",EDGE,"E76.0"),sQuery(id+"F9.wireOp",EDGE,"E78.0"),sQuery(id+"F9.wireOp",EDGE,"E79.0"),sQuery(id+"F9.wireOp",EDGE,"E80.0"),sQuery(id+"F9.wireOp",EDGE,"E81.0"),sQuery(id+"F9.wireOp",EDGE,"E82.0"),sQuery(id+"F9.wireOp",EDGE,"E83.0"),sQuery(id+"F9.wireOp",EDGE,"E84.0"),sQuery(id+"F9.wireOp",EDGE,"E85.0"),sQuery(id+"F9.wireOp",EDGE,"E87.0"),sQuery(id+"F9.wireOp",EDGE,"E89.0"),sQuery(id+"F9.wireOp",EDGE,"E90.0"),sQuery(id+"F9.wireOp",EDGE,"E91.0"),sQuery(id+"F9.wireOp",EDGE,"E92.0"),sQuery(id+"F9.wireOp",EDGE,"E93.0"),sQuery(id+"F9.wireOp",EDGE,"E94.0"),sQuery(id+"F9.wireOp",EDGE,"E95.0"),sQuery(id+"F9.wireOp",EDGE,"E96.0"),sQuery(id+"F9.wireOp",EDGE,"E97.0"),sQuery(id+"F9.wireOp",EDGE,"E98.0"),sQuery(id+"F9.wireOp",EDGE,"E99.0"),sQuery(id+"F9.wireOp",EDGE,"E100.0"),sQuery(id+"F9.wireOp",EDGE,"E101.0"),sQuery(id+"F9.wireOp",EDGE,"E102.0"),sQuery(id+"F9.wireOp",EDGE,"E103.0"),sQuery(id+"F9.wireOp",EDGE,"E104.0"),sQuery(id+"F9.wireOp",EDGE,"E105.0"),sQuery(id+"F9.wireOp",EDGE,"E106.0"),sQuery(id+"F9.wireOp",EDGE,"E107.0"),sQuery(id+"F9.wireOp",EDGE,"E109.0"),sQuery(id+"F9.wireOp",EDGE,"E110.0"),sQuery(id+"F9.wireOp",EDGE,"E111.0")])]});
            transform(context, id + "F11", {"entities" : qUnion([Q0]), "transformType" : TransformType.TRANSLATION_3D, "dx" : 0 * mm, "dy" : -39.2 * mm, "dz" : 4.1 * mm, "makeCopy" : false});
        }
    });
